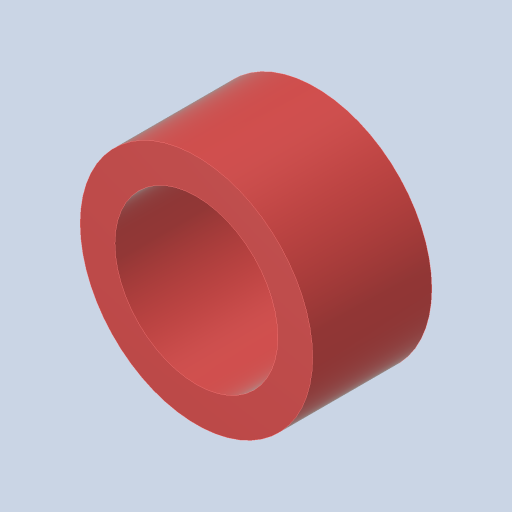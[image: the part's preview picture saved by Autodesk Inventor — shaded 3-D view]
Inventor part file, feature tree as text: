
AUTODESK INVENTOR PART (.ipt)
format: ipt  version: 2023.4 (Build 274418000, 418)  size: 123,904 bytes
history: native  units: in
note: dims shown in document units (in); Inventor stores cm internally (conversion verified against a paired STEP export)
features: extrude x1, sketch x1
ambient origin geometry x8: Origin, YZ Plane, XZ Plane, XY Plane, X Axis, Y Axis, Z Axis, Center Point
bodies: Solid1 (feature_tree)
feature tree (2):
  extrude  "Extrusion1"  Depth=0.428in
  sketch  "Sketch1"  dims[d0=0.585in d1=0.125in d2=0.428in d3=0.0in]
